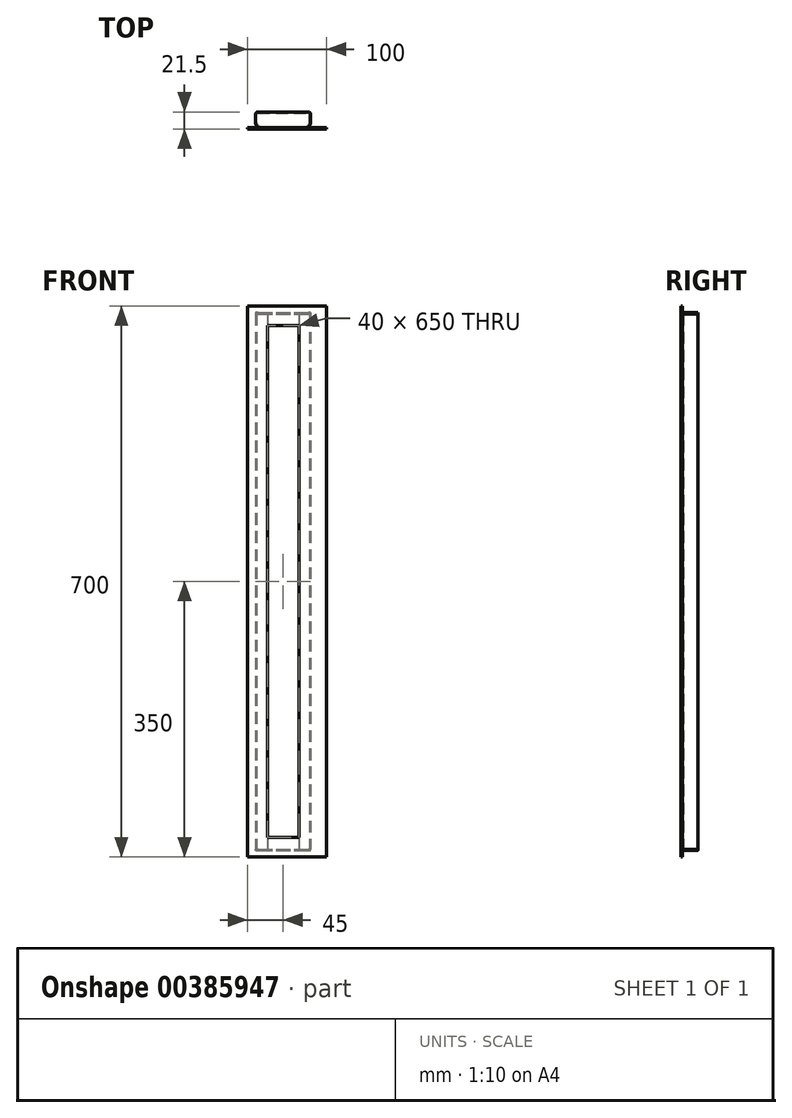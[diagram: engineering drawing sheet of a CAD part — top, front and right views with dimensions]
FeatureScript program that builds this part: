
annotation { "Feature Type Name" : "Feature", "Feature Type Description" : "" }
export const myFeature = defineFeature(function(context is Context, id is Id, definition is map)
    precondition{}
    {
        {
            var Q0;
            Q0=qCreatedBy(makeId("Front.planeOp"),FACE);
            var sketch = newSketch(context, id + "F0", { "sketchPlane" : qUnion([Q0])});
            skLineSegment(sketch, "E0.bottom", {"start": v(50, 350) * mm, "end": v(-50, 350) * mm});
            skLineSegment(sketch, "E0.top", {"start": v(50, -350) * mm, "end": v(-50, -350) * mm});
            skLineSegment(sketch, "E0.left", {"start": v(50, 350) * mm, "end": v(50, -350) * mm});
            skLineSegment(sketch, "E0.right", {"start": v(-50, 350) * mm, "end": v(-50, -350) * mm});
            skPoint(sketch, "E0.middle", {"position": v(0, 0) * mm});
            skLineSegment(sketch, "E1.bottom", {"start": v(-25, 325) * mm, "end": v(15, 325) * mm});
            skLineSegment(sketch, "E1.top", {"start": v(-25, -325) * mm, "end": v(15, -325) * mm});
            skLineSegment(sketch, "E1.left", {"start": v(-25, 325) * mm, "end": v(-25, -325) * mm});
            skLineSegment(sketch, "E1.right", {"start": v(15, 325) * mm, "end": v(15, -325) * mm});
            skSolve(sketch);
        }
        {
            var Q0;
            Q0 = qSketchRegion(id + "F0", true);
            extrude(context, id + "F1", {"entities" : qUnion([Q0]), "depth" : 1.5 * mm});
        }
        {
            var Q0;
            Q0=qCreatedBy(makeId("Top.planeOp"),FACE);
            var sketch = newSketch(context, id + "F2", { "sketchPlane" : qUnion([Q0])});
            skLineSegment(sketch, "E2.bottom", {"start": v(-33.5, 0) * mm, "end": v(23.5, 0) * mm});
            skLineSegment(sketch, "E2.top", {"start": v(-37, 20) * mm, "end": v(27, 20) * mm});
            skLineSegment(sketch, "E2.left", {"start": v(-40, 6.5) * mm, "end": v(-40, 17) * mm});
            skLineSegment(sketch, "E2.right", {"start": v(30, 6.5) * mm, "end": v(30, 17) * mm});
            skLineSegment(sketch, "E3.0", {"start": v(-37, 18.5) * mm, "end": v(27, 18.5) * mm});
            skLineSegment(sketch, "E3.1", {"start": v(-38.5, 6.5) * mm, "end": v(-38.5, 17) * mm});
            skLineSegment(sketch, "E3.2", {"start": v(-33.5, 1.5) * mm, "end": v(23.5, 1.5) * mm});
            skLineSegment(sketch, "E3.3", {"start": v(28.5, 6.5) * mm, "end": v(28.5, 17) * mm});
            skPoint(sketch, "E4.visualSharp", {"position": v(28.5, 1.5) * mm});
            skArc(sketch, "E4.filletArc", {"start": v(23.5, 1.5) * mm, "mid": v(27.04, 2.96) * mm, "end": v(28.5, 6.5) * mm});
            skPoint(sketch, "E5.visualSharp", {"position": v(30, 0) * mm});
            skArc(sketch, "E5.filletArc", {"start": v(23.5, 0) * mm, "mid": v(28.1, 1.9) * mm, "end": v(30, 6.5) * mm});
            skPoint(sketch, "E6.visualSharp", {"position": v(-38.5, 1.5) * mm});
            skArc(sketch, "E6.filletArc", {"start": v(-38.5, 6.5) * mm, "mid": v(-37.04, 2.96) * mm, "end": v(-33.5, 1.5) * mm});
            skPoint(sketch, "E7.visualSharp", {"position": v(-40, 0) * mm});
            skArc(sketch, "E7.filletArc", {"start": v(-40, 6.5) * mm, "mid": v(-38.1, 1.9) * mm, "end": v(-33.5, 0) * mm});
            skPoint(sketch, "E8.visualSharp", {"position": v(28.5, 18.5) * mm});
            skArc(sketch, "E8.filletArc", {"start": v(28.5, 17) * mm, "mid": v(28.06, 18.06) * mm, "end": v(27, 18.5) * mm});
            skPoint(sketch, "E9.visualSharp", {"position": v(-38.5, 18.5) * mm});
            skArc(sketch, "E9.filletArc", {"start": v(-37, 18.5) * mm, "mid": v(-38.06, 18.06) * mm, "end": v(-38.5, 17) * mm});
            skPoint(sketch, "E10.visualSharp", {"position": v(-40, 20) * mm});
            skArc(sketch, "E10.filletArc", {"start": v(-37, 20) * mm, "mid": v(-39.12, 19.12) * mm, "end": v(-40, 17) * mm});
            skPoint(sketch, "E11.visualSharp", {"position": v(30, 20) * mm});
            skArc(sketch, "E11.filletArc", {"start": v(30, 17) * mm, "mid": v(29.12, 19.12) * mm, "end": v(27, 20) * mm});
            skSolve(sketch);
        }
        {
            var Q0;
            Q0 = qSketchRegion(id + "F2", true);
            extrude(context, id + "F3", {"entities" : qUnion([Q0]), "endBound" : BoundingType.SYMMETRIC, "depth" : 680 * mm});
        }
        {
            var Q0;
            Q0=makeQuery(id+"F3.opExtrude","SWEPT_FACE",FACE,{"disambiguationData":[OSD([sQuery(id+"F2.wireOp",EDGE,"E2.bottom")])]});
            var sketch = newSketch(context, id + "F4", { "sketchPlane" : qUnion([Q0])});
            skLineSegment(sketch, "E12.0", {"start": v(15, 340) * mm, "end": v(15, -340) * mm});
            skLineSegment(sketch, "E12.1", {"start": v(-25, 340) * mm, "end": v(-25, -340) * mm});
            skLineSegment(sketch, "E13.0", {"start": v(-25, 340) * mm, "end": v(15, 340) * mm});
            skLineSegment(sketch, "E13.1", {"start": v(-25, -340) * mm, "end": v(15, -340) * mm});
            skPoint(sketch, "E14.orphan", {"position": v(-25, -325) * mm});
            skPoint(sketch, "E15.orphan", {"position": v(15, -325) * mm});
            skPoint(sketch, "E16.orphan", {"position": v(15, 325) * mm});
            skPoint(sketch, "E17.orphan", {"position": v(-25, 325) * mm});
            skPoint(sketch, "E18.orphan", {"position": v(23.5, -340) * mm});
            skPoint(sketch, "E19.orphan", {"position": v(-33.5, -340) * mm});
            skPoint(sketch, "E20.orphan", {"position": v(-33.5, 340) * mm});
            skPoint(sketch, "E21.orphan", {"position": v(23.5, 340) * mm});
            skSolve(sketch);
        }
        {
            var Q0;
            Q0 = qSketchRegion(id + "F4", true);
            extrude(context, id + "F5", {"entities" : qUnion([Q0]), "operationType" : NewBodyOperationType.REMOVE, "endBound" : BoundingType.UP_TO_NEXT, "oppositeDirection" : true, "depth" : 25 * mm});
        }
        {
            var Q0;
            Q0=makeQuery(id+"F3.opExtrude","CAP_FACE",FACE,{"disambiguationData":[OSD([sQuery(id+"F2.wireOp",EDGE,"E2.bottom"),sQuery(id+"F2.wireOp",EDGE,"E2.top"),sQuery(id+"F2.wireOp",EDGE,"E2.left"),sQuery(id+"F2.wireOp",EDGE,"E2.right"),sQuery(id+"F2.wireOp",EDGE,"E3.0"),sQuery(id+"F2.wireOp",EDGE,"E3.1"),sQuery(id+"F2.wireOp",EDGE,"E3.2"),sQuery(id+"F2.wireOp",EDGE,"E3.3"),sQuery(id+"F2.wireOp",EDGE,"E4.filletArc"),sQuery(id+"F2.wireOp",EDGE,"E5.filletArc"),sQuery(id+"F2.wireOp",EDGE,"E6.filletArc"),sQuery(id+"F2.wireOp",EDGE,"E7.filletArc"),sQuery(id+"F2.wireOp",EDGE,"E8.filletArc"),sQuery(id+"F2.wireOp",EDGE,"E9.filletArc"),sQuery(id+"F2.wireOp",EDGE,"E10.filletArc"),sQuery(id+"F2.wireOp",EDGE,"E11.filletArc")])],"isStart":false});
            var sketch = newSketch(context, id + "F6", { "sketchPlane" : qUnion([Q0])});
            skLineSegment(sketch, "E22.0", {"start": v(-37, 20) * mm, "end": v(27, 20) * mm});
            skArc(sketch, "E22.1", {"start": v(30, 17) * mm, "mid": v(29.12, 19.12) * mm, "end": v(27, 20) * mm});
            skLineSegment(sketch, "E22.2", {"start": v(30, 6.5) * mm, "end": v(30, 17) * mm});
            skArc(sketch, "E22.3", {"start": v(23.5, 0) * mm, "mid": v(28.1, 1.9) * mm, "end": v(30, 6.5) * mm});
            skLineSegment(sketch, "E22.4", {"start": v(-40, 6.5) * mm, "end": v(-40, 17) * mm});
            skArc(sketch, "E22.5", {"start": v(-37, 20) * mm, "mid": v(-39.12, 19.12) * mm, "end": v(-40, 17) * mm});
            skArc(sketch, "E22.6", {"start": v(-40, 6.5) * mm, "mid": v(-38.1, 1.9) * mm, "end": v(-33.5, 0) * mm});
            skLineSegment(sketch, "E23", {"start": v(-33.5, 0) * mm, "end": v(23.5, 0) * mm});
            skSolve(sketch);
        }
        {
            var Q0;
            Q0 = qSketchRegion(id + "F6", true);
            extrude(context, id + "F7", {"entities" : qUnion([Q0]), "depth" : 1.5 * mm});
        }
        {
            var Q0;
            Q0=makeQuery(id+"F7.opExtrude","SWEPT_BODY",BODY,{"disambiguationData":[OSD([sQuery(id+"F6.wireOp",EDGE,"E22.0"),sQuery(id+"F6.wireOp",EDGE,"E22.1"),sQuery(id+"F6.wireOp",EDGE,"E22.2"),sQuery(id+"F6.wireOp",EDGE,"E22.3"),sQuery(id+"F6.wireOp",EDGE,"E22.4"),sQuery(id+"F6.wireOp",EDGE,"E22.5"),sQuery(id+"F6.wireOp",EDGE,"E22.6"),sQuery(id+"F6.wireOp",EDGE,"E23")])]});
            var Q1;
            Q1=qCreatedBy(makeId("Top.planeOp"),FACE);
            mirror(context, id + "F8", {"entities" : qUnion([Q0]), "mirrorPlane" : qUnion([Q1])});
        }
    });
